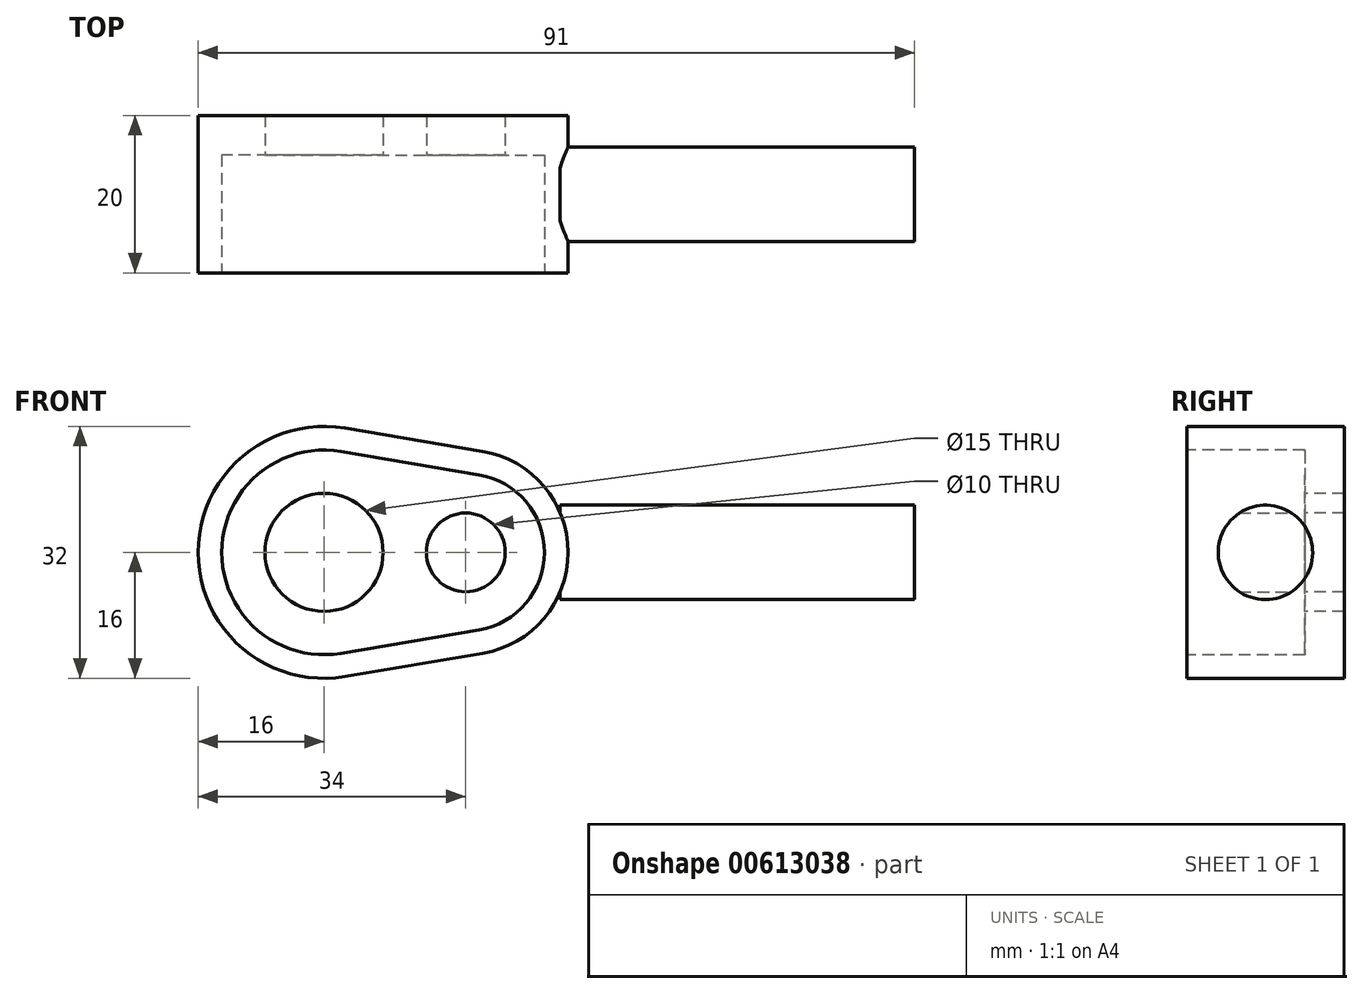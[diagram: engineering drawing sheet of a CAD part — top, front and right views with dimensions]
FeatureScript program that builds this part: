
annotation { "Feature Type Name" : "Feature", "Feature Type Description" : "" }
export const myFeature = defineFeature(function(context is Context, id is Id, definition is map)
    precondition{}
    {
        {
            var Q0;
            Q0=qCreatedBy(makeId("Front.planeOp"),FACE);
            var sketch = newSketch(context, id + "F0", { "sketchPlane" : qUnion([Q0])});
            skArc(sketch, "E0", {"start": v(2.67, -15.78) * mm, "mid": v(-16, 0) * mm, "end": v(2.67, 15.78) * mm});
            skArc(sketch, "E1", {"start": v(20.17, 12.82) * mm, "mid": v(31, 0) * mm, "end": v(20.17, -12.82) * mm});
            skLineSegment(sketch, "E2", {"start": v(2.67, 15.78) * mm, "end": v(20.17, 12.82) * mm});
            skLineSegment(sketch, "E3", {"start": v(2.67, -15.78) * mm, "end": v(20.17, -12.82) * mm});
            skSolve(sketch);
        }
        {
            var Q0;
            Q0 = qSketchRegion(id + "F0", true);
            extrude(context, id + "F1", {"entities" : qUnion([Q0]), "depth" : 20 * mm, "offsetDistance" : 25.4 * mm});
        }
        {
            var Q0;
            Q0=makeQuery(id+"F1.opExtrude","CAP_FACE",FACE,{"disambiguationData":[OSD([sQuery(id+"F0.wireOp",EDGE,"E0"),sQuery(id+"F0.wireOp",EDGE,"E1"),sQuery(id+"F0.wireOp",EDGE,"E2"),sQuery(id+"F0.wireOp",EDGE,"E3")])],"isStart":false});
            var sketch = newSketch(context, id + "F2", { "sketchPlane" : qUnion([Q0])});
            skLineSegment(sketch, "E4.0", {"start": v(2.17, 12.82) * mm, "end": v(19.67, 9.86) * mm});
            skArc(sketch, "E4.1", {"start": v(2.17, -12.82) * mm, "mid": v(-13, 0) * mm, "end": v(2.17, 12.82) * mm});
            skLineSegment(sketch, "E4.2", {"start": v(2.17, -12.82) * mm, "end": v(19.67, -9.86) * mm});
            skArc(sketch, "E4.3", {"start": v(19.67, 9.86) * mm, "mid": v(28, 0) * mm, "end": v(19.67, -9.86) * mm});
            skSolve(sketch);
        }
        {
            var Q0;
            Q0=makeQuery(id+"F2.imprint","IMPRINT",FACE,{"disambiguationData":[TD([[makeQuery(id+"F2.imprint","IMPRINT",EDGE,{"derivedFrom":sQuery(id+"F2.wireOp",EDGE,"E4.0")}),-1.0]])]});
            extrude(context, id + "F3", {"entities" : qUnion([Q0]), "operationType" : NewBodyOperationType.REMOVE, "oppositeDirection" : true, "depth" : 15 * mm, "offsetDistance" : 25.4 * mm});
        }
        {
            var Q0;
            Q0=makeQuery(id+"F3.boolean.opBoolean","COPY",FACE,{"derivedFrom":makeQuery(id+"F3.opExtrude","CAP_FACE",FACE,{"disambiguationData":[OSD([sQuery(id+"F2.wireOp",EDGE,"E4.0"),sQuery(id+"F2.wireOp",EDGE,"E4.1"),sQuery(id+"F2.wireOp",EDGE,"E4.2"),sQuery(id+"F2.wireOp",EDGE,"E4.3")])],"isStart":false})});
            var sketch = newSketch(context, id + "F4", { "sketchPlane" : qUnion([Q0])});
            skCircle(sketch, "E5", {"center": v(0, 0) * mm, "radius": 7.5 * mm});
            skCircle(sketch, "E6", {"center": v(18, 0) * mm, "radius": 5 * mm});
            skSolve(sketch);
        }
        {
            var Q0;
            Q0=makeQuery(id+"F4.imprint","IMPRINT",FACE,{"disambiguationData":[TD([[makeQuery(id+"F4.imprint","IMPRINT",EDGE,{"derivedFrom":sQuery(id+"F4.wireOp",EDGE,"E6")}),1.0]])]});
            var Q1;
            Q1=makeQuery(id+"F4.imprint","IMPRINT",FACE,{"disambiguationData":[TD([[makeQuery(id+"F4.imprint","IMPRINT",EDGE,{"derivedFrom":sQuery(id+"F4.wireOp",EDGE,"E5")}),1.0]])]});
            extrude(context, id + "F5", {"entities" : qUnion([Q0, Q1]), "operationType" : NewBodyOperationType.REMOVE, "oppositeDirection" : true, "depth" : 5 * mm, "offsetDistance" : 25.4 * mm});
        }
        {
            var Q0;
            Q0=qCreatedBy(makeId("Right.planeOp"),FACE);
            cPlane(context, id + "F6", {"entities" : qUnion([Q0]), "cplaneType" : CPlaneType.OFFSET, "offset" : 30 * mm, "width" : 152.4 * mm, "height" : 152.4 * mm});
        }
        {
            var Q0;
            Q0=qCreatedBy(id+"F6.planeOp",FACE);
            var sketch = newSketch(context, id + "F7", { "sketchPlane" : qUnion([Q0])});
            skCircle(sketch, "E7", {"center": v(-10, 0) * mm, "radius": 6 * mm});
            skSolve(sketch);
        }
        {
            var Q0;
            Q0 = qSketchRegion(id + "F7", true);
            extrude(context, id + "F8", {"entities" : qUnion([Q0]), "operationType" : NewBodyOperationType.ADD, "depth" : 45 * mm, "offsetDistance" : 25.4 * mm});
        }
    });
